# Revit family: Plumbing-Flushometer-Sloan-Valve-ROYAL-190Z
name_source: partatom
category: Plumbing Fixtures
units: mm (PartAtom-declared; Revit-internal decimal feet)

## family parameters
Cut with Voids When Loaded = Yes
Host = Face
OmniClass Number = 23.45.05.14.99
OmniClass Title = Other Sanitary Washing Plumbing Fixtures
Part Type = Normal
Room Calculation Point = No
Round Connector Dimension = Use Diameter
Shared = No

## types (1)
- Not a Type - Load Type Catalog!
    3" Oscillating Button = Yes
    Assembly Code = D2020300
    CW Connection = Yes
    CWFU = 0
    Centerline of Supply from Top of Fixture = 14 1/2"
    Centerline of Supply to Centerline of Valve = 4 3/4"
    Default Elevation = 0"
    Description = 1.0 gpf, Rough Brass Finish, Fixture Connection Rear Spud, Single Flush, 2.75 L Dimension, 3" Metal Oscillating Push Button, Royal® Concealed Manual Urinal Flushometer.
    Edition number = 1
    Flush Rate = 1.0 gpf (3.8 Lpf)
    Flushometer Material = Sloan Valve - Finish - Rough Brass
    HW Connection = No
    HWFU = 0
    Keynote = 15410
    L Dimension = 2 3/4"
    Manufacturer = Sloan Valve
    Model = Model not specified - Load type catalog!
    Operating Water Pressure = 15 – 80 PSI (103 – 552 kPa)
    Part Number = 3913078
    Product Material = Sloan Valve - Finish - Rough Brass
    URL = www.sloanvalve.com
    Valve Pressure Drop = 0.00 psi
    Vent Connection = No
    WFU = 0
    Waste Connection = No
    Water Inlet Connection Description = Water Inlet Connection
    Water Inlet Connection Diameter = 1"
    z_Button = Yes
    z_Connector Offset = 7 1/4"
    z_Push Button = No

## geometry (parser evidence)
native form markers: Sweep x2
no freeform markers — native parametric forms only
